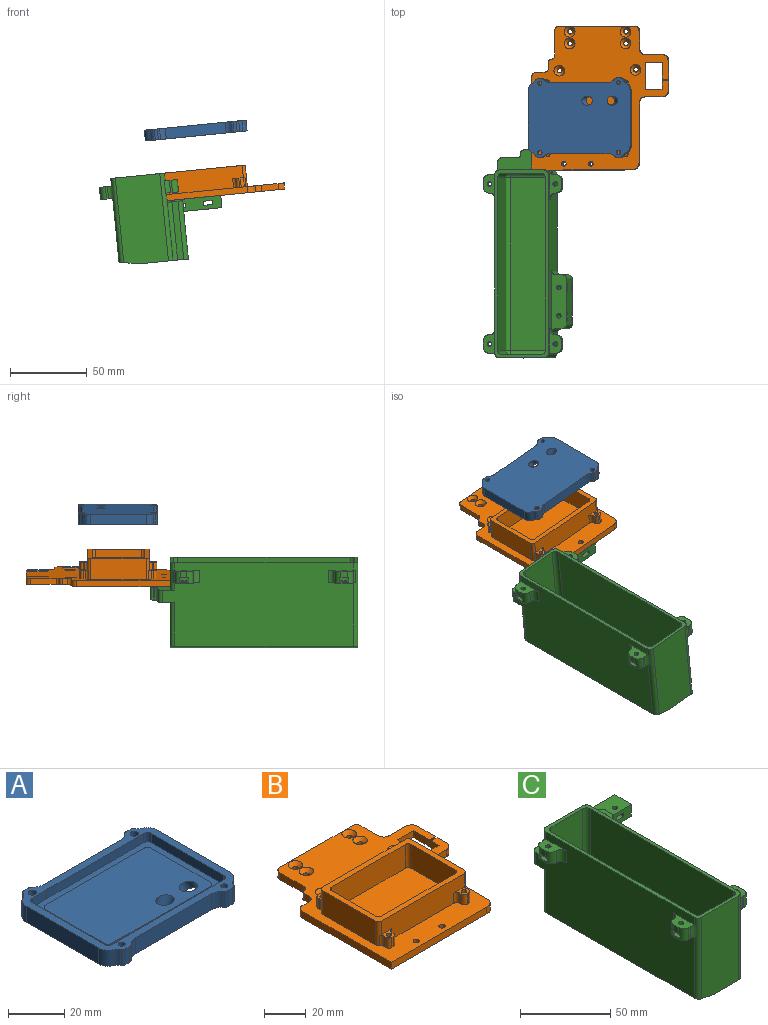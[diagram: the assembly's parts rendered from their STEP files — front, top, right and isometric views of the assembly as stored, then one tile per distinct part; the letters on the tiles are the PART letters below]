
ASSEMBLY  parts=3 mates=2
PART A: 55 faces, bbox 66.4x51.5x10 mm
  f0: plane 60.4x40.4mm, normal (0,0,1), area 653.3mm2, adj f1,f2,f3,f4,f5,f6,f7,f8
  f1: plane 7.5x4mm, normal (0,-1,0), area 30mm2, adj f0,f2,f31,f34
  f2: plane 48.9x4mm, normal (0,-1,0), area 195.6mm2, adj f0,f1,f3,f34
  f3: cylinder r=2mm len=4mm, axis (0,0,-1), area 12.6mm2, adj f0,f2,f4,f34
  f4: plane 36.4x4mm, normal (-1,0,0), area 145.6mm2, adj f0,f3,f5,f34
  f5: cylinder r=2mm len=4mm, axis (0,0,-1), area 12.6mm2, adj f0,f4,f6,f34
  f6: plane 56.4x4mm, normal (0,1,0), area 225.6mm2, adj f0,f5,f7,f34
  f7: cylinder r=2mm len=4mm, axis (0,0,-1), area 12.6mm2, adj f0,f6,f8,f34
  f8: plane 36.4x4mm, normal (1,0,0), area 145.6mm2, adj f0,f7,f31,f34
  f9: plane 39.03x7mm, normal (0,1,0), area 273.2mm2, adj f34,f35,f45,f46
  f10: cylinder r=2mm len=7mm, axis (0,0,-1), area 11.7mm2, adj f11,f34,f35,f46
  f11: plane 7x2mm, normal (0,1,0), area 14mm2, adj f10,f12,f34,f35
  f12: cylinder r=2mm len=7mm, axis (0,0,-1), area 14.3mm2, adj f11,f34,f35,f47
  f13: cylinder r=5mm len=7mm, axis (0,0,-1), area 38.7mm2, adj f14,f34,f35,f47
  f14: plane 36.4x7mm, normal (-1,0,0), area 254.8mm2, adj f13,f15,f34,f35
  f15: cylinder r=5mm len=7mm, axis (0,0,-1), area 38.7mm2, adj f14,f34,f35,f48
  f16: cylinder r=2mm len=7mm, axis (0,0,-1), area 14.3mm2, adj f17,f34,f35,f48
  f17: plane 7x2mm, normal (0,-1,0), area 14mm2, adj f16,f18,f34,f35
  f18: cylinder r=2mm len=7mm, axis (0,0,-1), area 11.7mm2, adj f17,f34,f35,f49
  f19: plane 38.61x7mm, normal (0,-1,0), area 270.3mm2, adj f34,f35,f49,f50
  f20: cylinder r=2mm len=7mm, axis (0,0,-1), area 13mm2, adj f21,f34,f35,f50
  f21: plane 7x2mm, normal (0,-1,0), area 14mm2, adj f20,f22,f34,f35
  f22: cylinder r=2mm len=7mm, axis (0,0,-1), area 15.9mm2, adj f21,f34,f35,f51
  f23: cylinder r=5mm len=7mm, axis (0,0,-1), area 37.3mm2, adj f24,f34,f35,f51
  f24: plane 36.4x7mm, normal (1,0,0), area 254.8mm2, adj f23,f25,f34,f35
  f25: cylinder r=5mm len=7mm, axis (0,0,-1), area 38.7mm2, adj f24,f34,f35,f52
  f26: cylinder r=2mm len=7mm, axis (0,0,-1), area 14.3mm2, adj f27,f34,f35,f52
  f27: plane 7x2mm, normal (0,1,0), area 14mm2, adj f26,f32,f34,f35
  f28: cylinder r=1.25mm len=7mm, axis (0,0,-1), area 55mm2, adj f34,f35
  f29: cylinder r=1.25mm len=7mm, axis (0,0,-1), area 55mm2, adj f34,f35
  f30: cylinder r=1.5mm len=7mm, axis (0,0,-1), area 66mm2, adj f34,f35
  f31: cylinder r=2mm len=4mm, axis (0,0,-1), area 12.6mm2, adj f0,f1,f8,f34
  f32: cylinder r=2mm len=7mm, axis (0,0,-1), area 11.7mm2, adj f27,f34,f35,f45
  f33: cylinder r=1.5mm len=7mm, axis (0,0,-1), area 66mm2, adj f34,f35
  f34: plane 66.4x51.5mm, normal (0,0,1), area 658.1mm2, adj f1,f2,f3,f4,f5,f6,f7,f8
  f35: plane 66.4x51.5mm, normal (0,0,-1), area 3029.5mm2, adj f9,f10,f11,f12,f13,f14,f15,f16
  f36: plane 29.4x1mm, normal (-1,0,0), area 29.4mm2, adj f0,f37,f43,f44
  f37: cylinder r=2mm len=2mm, axis (0,0,-1), area 3.1mm2, adj f0,f36,f38,f44
  f38: plane 49.5x1mm, normal (0,-1,0), area 49.5mm2, adj f0,f37,f39,f44
  f39: cylinder r=2mm len=2mm, axis (0,0,-1), area 3.1mm2, adj f0,f38,f40,f44
  f40: plane 29.4x1mm, normal (1,0,0), area 29.4mm2, adj f0,f39,f41,f44
  f41: cylinder r=2mm len=2mm, axis (0,0,-1), area 3.1mm2, adj f0,f40,f42,f44
  f42: plane 49.5x1mm, normal (0,1,0), area 49.5mm2, adj f0,f41,f43,f44
  f43: cylinder r=2mm len=2mm, axis (0,0,-1), area 3.1mm2, adj f0,f36,f42,f44
  f44: plane 53.5x33.4mm, normal (0,0,1), area 1718.2mm2, adj f36,f37,f38,f39,f40,f41,f42,f43
  f45: cylinder r=5mm len=7mm, axis (0,0,-1), area 29.2mm2, adj f9,f32,f34,f35
  f46: cylinder r=5mm len=7mm, axis (0,0,-1), area 29.2mm2, adj f9,f10,f34,f35
  f47: cylinder r=5mm len=7mm, axis (0,0,1), area 19.6mm2, adj f12,f13,f34,f35
  f48: cylinder r=5mm len=7mm, axis (0,0,1), area 19.6mm2, adj f15,f16,f34,f35
  f49: cylinder r=5mm len=7mm, axis (0,0,-1), area 29.2mm2, adj f18,f19,f34,f35
  f50: cylinder r=5mm len=7mm, axis (0,0,-1), area 32.5mm2, adj f19,f20,f34,f35
  f51: cylinder r=5mm len=7mm, axis (0,0,1), area 22.1mm2, adj f22,f23,f34,f35
  f52: cylinder r=5mm len=7mm, axis (0,0,1), area 19.6mm2, adj f25,f26,f34,f35
  f53: cylinder r=3mm len=10.02mm, axis (0.5,0,-0.87), area 87.1mm2, adj f35,f44
  f54: cylinder r=3mm len=10.02mm, axis (-0.5,0,-0.87), area 87.1mm2, adj f35,f44
PART B: 103 faces, bbox 89x93.5x18 mm
  f0: plane 93.5x89mm, normal (0,0,-1), area 6273mm2, adj f1,f3,f4,f5,f6,f10,f11,f12
  f1: plane 12x4mm, normal (1,0,0), area 43.4mm2, adj f0,f2,f92,f98
  f2: plane 93.5x89mm, normal (0,0,1), area 3705.7mm2, adj f1,f3,f4,f5,f6,f10,f11,f12
  f3: plane 11x4mm, normal (-1,0,0), area 39.4mm2, adj f0,f2,f95,f98
  f4: plane 38.5x4mm, normal (1,0,0), area 154mm2, adj f0,f2,f88,f102
  f5: plane 4x3.5mm, normal (-1,0,0), area 14mm2, adj f0,f2,f13,f76
  f6: plane 17.5x4mm, normal (1,0,0), area 70mm2, adj f0,f2,f87,f95
  f7: plane 8x5.27mm, normal (0,0,1), area 19.6mm2, adj f25,f53,f54,f55,f56,f57,f58,f59
  f8: plane 8x5.27mm, normal (0,0,1), area 19.6mm2, adj f43,f44,f45,f46,f47,f48,f49,f50
  f9: plane 8x5.27mm, normal (0,0,1), area 19.6mm2, adj f25,f26,f27,f28,f29,f30,f31,f32
  f10: plane 49x4mm, normal (0,1,0), area 196mm2, adj f0,f2,f11,f23
  f11: cylinder r=3mm len=4mm, axis (0,0,-1), area 18.8mm2, adj f0,f2,f10,f12
  f12: plane 16.5x4mm, normal (-1,0,0), area 66mm2, adj f0,f2,f11,f77
  f13: cylinder r=3mm len=4mm, axis (0,0,-1), area 18.8mm2, adj f0,f2,f5,f14
  f14: plane 5x4mm, normal (0,1,0), area 20mm2, adj f0,f2,f13,f15
  f15: cylinder r=3mm len=4mm, axis (0,0,-1), area 18.8mm2, adj f0,f2,f14,f16
  f16: plane 60.5x4mm, normal (-1,0,0), area 242mm2, adj f0,f2,f15,f78
  f17: plane 11.5x4mm, normal (1,0,0), area 46mm2, adj f0,f2,f23,f94
  f18: cylinder r=1.5mm len=3mm, axis (0,0,-1), area 18.8mm2, adj f0,f81
  f19: cylinder r=1.5mm len=3mm, axis (0,0,-1), area 18.8mm2, adj f0,f84
  f20: cylinder r=1.5mm len=3mm, axis (0,0,-1), area 18.8mm2, adj f0,f85
  f21: cylinder r=1.5mm len=3mm, axis (0,0,-1), area 18.8mm2, adj f0,f82
  f22: cylinder r=1.5mm len=3mm, axis (0,0,-1), area 18.8mm2, adj f0,f83
  f23: cylinder r=3mm len=4mm, axis (0,0,-1), area 18.8mm2, adj f0,f2,f10,f17
  f24: cylinder r=1.5mm len=3mm, axis (0,0,-1), area 18.8mm2, adj f0,f86
  f25: plane 56x14mm, normal (0,1,0), area 700mm2, adj f2,f7,f9,f26,f33,f53,f63,f66
  f26: cylinder r=2mm len=6mm, axis (0,0,-1), area 18.8mm2, adj f2,f9,f25,f27
  f27: plane 6x1mm, normal (1,0,0), area 6mm2, adj f2,f9,f26,f28
  f28: cylinder r=2mm len=6mm, axis (0,0,-1), area 18.8mm2, adj f2,f9,f27,f29
  f29: plane 6x1mm, normal (0,1,0), area 6mm2, adj f2,f9,f28,f30
  f30: cylinder r=2mm len=6mm, axis (0,0,-1), area 18.8mm2, adj f2,f9,f29,f31
  f31: plane 6x1.54mm, normal (-1,0,0), area 9.2mm2, adj f2,f9,f30,f32
  f32: cylinder r=2mm len=6mm, axis (0,0,-1), area 12.6mm2, adj f2,f9,f31,f33
  f33: cylinder r=2mm len=14mm, axis (0,0,-1), area 37.7mm2, adj f2,f9,f25,f32,f34,f66
  f34: plane 36x14mm, normal (-1,0,0), area 504mm2, adj f2,f33,f35,f66
  f35: cylinder r=2mm len=14mm, axis (0,0,-1), area 37.7mm2, adj f2,f34,f36,f43,f65,f66
  f36: cylinder r=2mm len=6mm, axis (0,0,-1), area 12.6mm2, adj f2,f35,f37,f65
  f37: plane 6x1.54mm, normal (-1,0,0), area 9.2mm2, adj f2,f36,f38,f65
  f38: cylinder r=2mm len=6mm, axis (0,0,-1), area 18.8mm2, adj f2,f37,f39,f65
  f39: plane 6x1mm, normal (0,-1,0), area 6mm2, adj f2,f38,f40,f65
  f40: cylinder r=2mm len=6mm, axis (0,0,-1), area 18.8mm2, adj f2,f39,f41,f65
  f41: plane 6x1mm, normal (1,0,0), area 6mm2, adj f2,f40,f42,f65
  f42: cylinder r=2mm len=6mm, axis (0,0,-1), area 18.8mm2, adj f2,f41,f43,f65
  f43: plane 56x14mm, normal (0,-1,0), area 700mm2, adj f2,f8,f35,f42,f44,f51,f65,f66
  f44: cylinder r=2mm len=6mm, axis (0,0,-1), area 18.8mm2, adj f2,f8,f43,f45
  f45: plane 6x1mm, normal (-1,0,0), area 6mm2, adj f2,f8,f44,f46
  f46: cylinder r=2mm len=6mm, axis (0,0,-1), area 18.8mm2, adj f2,f8,f45,f47
  f47: plane 6x1mm, normal (0,-1,0), area 6mm2, adj f2,f8,f46,f48
  f48: cylinder r=2mm len=6mm, axis (0,0,-1), area 18.8mm2, adj f2,f8,f47,f49
  f49: plane 6x1.54mm, normal (1,0,0), area 9.2mm2, adj f2,f8,f48,f50
  f50: cylinder r=2mm len=6mm, axis (0,0,-1), area 12.6mm2, adj f2,f8,f49,f51
  f51: cylinder r=2mm len=14mm, axis (0,0,-1), area 37.7mm2, adj f2,f8,f43,f50,f52,f66
  f52: plane 36x14mm, normal (1,0,0), area 504mm2, adj f2,f51,f53,f66
  f53: cylinder r=2mm len=14mm, axis (0,0,-1), area 37.7mm2, adj f2,f7,f25,f52,f54,f66
  f54: cylinder r=2mm len=6mm, axis (0,0,-1), area 12.6mm2, adj f2,f7,f53,f55
  f55: plane 6x1.54mm, normal (1,0,0), area 9.2mm2, adj f2,f7,f54,f56
  f56: cylinder r=2mm len=6mm, axis (0,0,-1), area 18.8mm2, adj f2,f7,f55,f57
  f57: plane 6x1mm, normal (0,1,0), area 6mm2, adj f2,f7,f56,f58
  f58: cylinder r=2mm len=6mm, axis (0,0,-1), area 18.8mm2, adj f2,f7,f57,f59
  f59: plane 6x1mm, normal (-1,0,0), area 6mm2, adj f2,f7,f58,f63
  f60: cylinder r=1.25mm len=10mm, axis (0,0,-1), area 78.5mm2, adj f0,f65
  f61: cylinder r=1.25mm len=10mm, axis (0,0,-1), area 78.5mm2, adj f0,f8
  f62: cylinder r=1.25mm len=10mm, axis (0,0,-1), area 78.5mm2, adj f0,f7
  f63: cylinder r=2mm len=6mm, axis (0,0,-1), area 18.8mm2, adj f2,f7,f25,f59
  f64: cylinder r=1.25mm len=10mm, axis (0,0,-1), area 78.5mm2, adj f0,f9
  f65: plane 8x5.27mm, normal (0,0,1), area 19.6mm2, adj f35,f36,f37,f38,f39,f40,f41,f42
  f66: plane 60x40mm, normal (0,0,1), area 564mm2, adj f25,f33,f34,f35,f43,f51,f52,f53
  f67: plane 54x34mm, normal (0,0,1), area 1736.6mm2, adj f68,f69,f70,f71,f72,f73,f74,f75
  f68: plane 50x18mm, normal (0,1,0), area 748mm2, adj f0,f66,f67,f69,f75,f99,f101
  f69: cylinder r=2mm len=14mm, axis (0,0,-1), area 44mm2, adj f66,f67,f68,f70
  f70: plane 30x14mm, normal (-1,0,0), area 420mm2, adj f66,f67,f69,f71
  f71: cylinder r=2mm len=14mm, axis (0,0,-1), area 44mm2, adj f66,f67,f70,f72
  f72: plane 50x14mm, normal (0,-1,0), area 700mm2, adj f66,f67,f71,f73
  f73: cylinder r=2mm len=14mm, axis (0,0,-1), area 44mm2, adj f66,f67,f72,f74
  f74: plane 30x14mm, normal (1,0,0), area 420mm2, adj f66,f67,f73,f75
  f75: cylinder r=2mm len=14mm, axis (0,0,-1), area 44mm2, adj f66,f67,f68,f74
  f76: cylinder r=2mm len=4mm, axis (0,0,1), area 12.6mm2, adj f0,f2,f5,f77
  f77: cylinder r=2mm len=4mm, axis (0,0,1), area 12.6mm2, adj f0,f2,f12,f76
  f78: plane 65x4mm, normal (0,-1,0), area 260mm2, adj f0,f2,f16,f102
  f79: cylinder r=1.5mm len=4mm, axis (0,0,1), area 37.7mm2, adj f0,f2
  f80: cylinder r=1.5mm len=4mm, axis (0,0,1), area 37.7mm2, adj f0,f2
  f81: cone r=1.5mm half-angle=45deg, axis (0,0,1), area 44.4mm2, adj f2,f18
  f82: cone r=1.5mm half-angle=45deg, axis (0,0,1), area 44.4mm2, adj f2,f21
  f83: cone r=1.5mm half-angle=45deg, axis (0,0,1), area 44.4mm2, adj f2,f22
  f84: cone r=1.5mm half-angle=45deg, axis (0,0,1), area 44.4mm2, adj f2,f19
  f85: cone r=1.5mm half-angle=45deg, axis (0,0,1), area 44.4mm2, adj f2,f20
  f86: cone r=1.5mm half-angle=45deg, axis (0,0,1), area 44.4mm2, adj f2,f24
  f87: plane 11x4mm, normal (0,1,0), area 44mm2, adj f0,f2,f6,f96
  f88: cylinder r=4mm len=4mm, axis (0,0,1), area 25.1mm2, adj f0,f2,f4,f89
  f89: plane 11x4mm, normal (0,-1,0), area 44mm2, adj f0,f2,f88,f90
  f90: cylinder r=4mm len=4mm, axis (0,0,1), area 25.1mm2, adj f0,f2,f89,f91
  f91: plane 8.65x4mm, normal (1,0,0), area 30mm2, adj f0,f2,f90,f97
  f92: cylinder r=4mm len=4mm, axis (0,0,1), area 25.1mm2, adj f0,f1,f2,f93
  f93: plane 11x4mm, normal (0,1,0), area 44mm2, adj f0,f2,f92,f94
  f94: cylinder r=4mm len=4mm, axis (0,0,1), area 25.1mm2, adj f0,f2,f17,f93
  f95: plane 11x4mm, normal (0,-1,0), area 44mm2, adj f0,f2,f3,f6
  f96: plane 7.65x4mm, normal (-1,0,0), area 26mm2, adj f0,f2,f87,f97
  f97: plane 4x4mm, normal (0,0.87,0.5), area 18.5mm2, adj f0,f2,f91,f96
  f98: plane 4x4mm, normal (0,-0.87,-0.5), area 18.5mm2, adj f0,f1,f2,f3
  f99: plane 8x4mm, normal (-1,0,0), area 32mm2, adj f0,f67,f68,f100
  f100: plane 12x4mm, normal (0,-1,0), area 48mm2, adj f0,f67,f99,f101
  f101: plane 8x4mm, normal (1,0,0), area 32mm2, adj f0,f67,f68,f100
  f102: cylinder r=5mm len=5mm, axis (0,0,1), area 31.4mm2, adj f0,f2,f4,f78
PART C: 159 faces, bbox 78x135x57 mm
  f0: plane 38x29mm, normal (1,0,0), area 1040.4mm2, adj f29,f50,f51,f52,f53,f57,f58,f59
  f1: plane 31x29mm, normal (0,1,0), area 747.9mm2, adj f20,f29,f32,f78,f129,f150,f151,f152
  f2: plane 4.3x4mm, normal (-1,0,0), area 17.2mm2, adj f4,f5,f106,f148
  f3: plane 4x1mm, normal (-1,0,0), area 4mm2, adj f7,f8,f114,f142
  f4: cylinder r=4mm len=8mm, axis (0,0,-1), area 48mm2, adj f2,f102,f103,f106,f107,f145,f147,f148
  f5: cylinder r=4mm len=8mm, axis (0,0,-1), area 48mm2, adj f2,f103,f105,f106,f107,f146,f147,f148
  f6: cylinder r=1.5mm len=3mm, axis (0,0,-1), area 9.4mm2, adj f107,f147
  f7: cylinder r=4mm len=8mm, axis (0,0,-1), area 48mm2, adj f3,f110,f111,f113,f114,f140,f142,f143
  f8: cylinder r=4mm len=8mm, axis (0,0,-1), area 48mm2, adj f3,f108,f111,f113,f114,f141,f142,f143
  f9: cylinder r=1.5mm len=3mm, axis (0,0,-1), area 9.4mm2, adj f114,f142
  f10: plane 4.3x4mm, normal (1,0,0), area 17.2mm2, adj f12,f13,f115,f138
  f11: plane 4x1mm, normal (1,0,0), area 4mm2, adj f15,f17,f123,f131
  f12: cylinder r=4mm len=8mm, axis (0,0,-1), area 48mm2, adj f10,f115,f116,f118,f119,f135,f137,f138
  f13: cylinder r=4mm len=8mm, axis (0,0,-1), area 48mm2, adj f10,f115,f116,f119,f121,f136,f137,f138
  f14: cylinder r=1.5mm len=3mm, axis (0,0,-1), area 9.4mm2, adj f116,f137
  f15: cylinder r=4mm len=8mm, axis (0,0,-1), area 48mm2, adj f11,f122,f123,f124,f125,f130,f131,f132
  f16: cylinder r=1.5mm len=3mm, axis (0,0,-1), area 9.4mm2, adj f123,f131
  f17: cylinder r=4mm len=8mm, axis (0,0,-1), area 48mm2, adj f11,f122,f123,f124,f127,f131,f132,f133
  f18: plane 57x29mm, normal (0,-1,0), area 1644.2mm2, adj f21,f29,f80,f83,f129
  f19: plane 124x54.71mm, normal (-1,0,0), area 6154.1mm2, adj f20,f21,f30,f32,f79,f82,f83,f105
  f20: cylinder r=3mm len=29.24mm, axis (0,0,1), area 136.2mm2, adj f1,f19,f32,f129
  f21: cylinder r=3mm len=55.24mm, axis (0,0,-1), area 244.1mm2, adj f18,f19,f83,f109,f113,f114,f129
  f22: plane 35x8mm, normal (0,-1,0), area 249.2mm2, adj f27,f30,f31,f32,f36,f37,f38,f39
  f23: cylinder r=1.5mm len=3mm, axis (0,0,1), area 25mm2, adj f32,f40
  f24: cylinder r=1.5mm len=3mm, axis (0,0,1), area 25mm2, adj f32,f36
  f25: plane 53x8mm, normal (0,1,0), area 393.2mm2, adj f30,f31,f32,f36,f37,f38,f39,f40
  f26: plane 10x8mm, normal (0,1,0), area 80mm2, adj f30,f32,f44,f79
  f27: plane 119x57mm, normal (1,0,0), area 4822mm2, adj f22,f29,f30,f32,f74,f75,f78,f80
  f28: plane 29x18mm, normal (0,1,0), area 522mm2, adj f30,f81,f82,f83
  f29: plane 122x32mm, normal (0,0,-1), area 3030.1mm2, adj f0,f1,f18,f27,f46,f47,f74,f75
  f30: plane 70x16mm, normal (0,0,1), area 822.8mm2, adj f19,f22,f25,f26,f27,f28,f31,f33
  f31: plane 13x8mm, normal (1,0,0), area 104mm2, adj f22,f25,f30,f32
  f32: plane 70x16mm, normal (0,0,-1), area 822.8mm2, adj f1,f19,f20,f22,f23,f24,f25,f26
  f33: cylinder r=1.5mm len=3mm, axis (0,0,1), area 25mm2, adj f30,f42
  f34: cylinder r=1.5mm len=3mm, axis (0,0,1), area 25mm2, adj f30,f38
  f35: plane 8x1mm, normal (-1,0,0), area 8mm2, adj f30,f32,f44,f45
  f36: plane 13x5.7mm, normal (0,0,1), area 67mm2, adj f22,f24,f25,f37,f39
  f37: plane 13x2.7mm, normal (1,0,0), area 35.1mm2, adj f22,f25,f36,f38
  f38: plane 13x5.7mm, normal (0,0,-1), area 67mm2, adj f22,f25,f34,f37,f39
  f39: plane 13x2.7mm, normal (-1,0,0), area 35.1mm2, adj f22,f25,f36,f38
  f40: plane 13x5.7mm, normal (0,0,1), area 67mm2, adj f22,f23,f25,f41,f43
  f41: plane 13x2.7mm, normal (1,0,0), area 35.1mm2, adj f22,f25,f40,f42
  f42: plane 13x5.7mm, normal (0,0,-1), area 67mm2, adj f22,f25,f33,f41,f43
  f43: plane 13x2.7mm, normal (-1,0,0), area 35.1mm2, adj f22,f25,f40,f42
  f44: cylinder r=2mm len=8mm, axis (0,0,1), area 25.1mm2, adj f26,f30,f32,f35
  f45: cylinder r=2mm len=8mm, axis (0,0,-1), area 25.1mm2, adj f25,f30,f32,f35
  f46: plane 38x4mm, normal (0,1,0), area 152mm2, adj f29,f75,f77,f158
  f47: plane 38x4mm, normal (0,-1,0), area 152mm2, adj f29,f74,f76,f158
  f48: cylinder r=1.5mm len=4mm, axis (0,0,1), area 37.7mm2, adj f58,f158
  f49: cylinder r=1.5mm len=4mm, axis (0,0,1), area 37.7mm2, adj f51,f158
  f50: plane 8x5.7mm, normal (0,0,1), area 38.5mm2, adj f0,f52,f53,f54,f56
  f51: plane 8x5.7mm, normal (0,0,-1), area 38.5mm2, adj f0,f49,f52,f53,f54
  f52: plane 8x2.7mm, normal (0,-1,0), area 21.6mm2, adj f0,f50,f51,f54
  f53: plane 8x2.7mm, normal (0,1,0), area 21.6mm2, adj f0,f50,f51,f54
  f54: plane 5.7x2.7mm, normal (1,0,0), area 15.4mm2, adj f50,f51,f52,f53
  f55: plane 3x3mm, normal (0,0,1), area 7.1mm2, adj f56
  f56: cylinder r=1.5mm len=17.3mm, axis (0,0,1), area 163mm2, adj f50,f55
  f57: plane 8x5.7mm, normal (0,0,1), area 38.5mm2, adj f0,f59,f60,f61,f63
  f58: plane 8x5.7mm, normal (0,0,-1), area 38.5mm2, adj f0,f48,f59,f60,f61
  f59: plane 8x2.7mm, normal (0,-1,0), area 21.6mm2, adj f0,f57,f58,f61
  f60: plane 8x2.7mm, normal (0,1,0), area 21.6mm2, adj f0,f57,f58,f61
  f61: plane 5.7x2.7mm, normal (1,0,0), area 15.4mm2, adj f57,f58,f59,f60
  f62: plane 3x3mm, normal (0,0,1), area 7.1mm2, adj f63
  f63: cylinder r=1.5mm len=17.3mm, axis (0,0,1), area 163mm2, adj f57,f62
  f64: plane 8x5.7mm, normal (0,0,1), area 45.6mm2, adj f0,f65,f67,f68
  f65: plane 8x2.7mm, normal (0,-1,0), area 21.6mm2, adj f0,f64,f66,f68
  f66: plane 8x5.7mm, normal (0,0,-1), area 45.6mm2, adj f0,f65,f67,f68
  f67: plane 8x2.7mm, normal (0,1,0), area 21.6mm2, adj f0,f64,f66,f68
  f68: plane 5.7x2.7mm, normal (1,0,0), area 15.4mm2, adj f64,f65,f66,f67
  f69: plane 8x5.7mm, normal (0,0,1), area 45.6mm2, adj f0,f70,f72,f73
  f70: plane 8x2.7mm, normal (0,-1,0), area 21.6mm2, adj f0,f69,f71,f73
  f71: plane 8x5.7mm, normal (0,0,-1), area 45.6mm2, adj f0,f70,f72,f73
  f72: plane 8x2.7mm, normal (0,1,0), area 21.6mm2, adj f0,f69,f71,f73
  f73: plane 5.7x2.7mm, normal (1,0,0), area 15.4mm2, adj f69,f70,f71,f72
  f74: cylinder r=3mm len=38mm, axis (0,0,1), area 179.1mm2, adj f27,f29,f47,f158
  f75: cylinder r=3mm len=38mm, axis (0,0,-1), area 179.1mm2, adj f27,f29,f46,f158
  f76: cylinder r=3mm len=38mm, axis (0,0,1), area 179.1mm2, adj f0,f29,f47,f158
  f77: cylinder r=3mm len=38mm, axis (0,0,-1), area 179.1mm2, adj f0,f29,f46,f158
  f78: cylinder r=3mm len=31mm, axis (0,0,-1), area 146.1mm2, adj f1,f27,f29,f32
  f79: cylinder r=3mm len=8mm, axis (0,0,-1), area 37.7mm2, adj f19,f26,f30,f32
  f80: cylinder r=3mm len=57mm, axis (0,0,1), area 254mm2, adj f18,f27,f29,f83,f115,f116,f117
  f81: cylinder r=3mm len=18mm, axis (0,0,-1), area 70.2mm2, adj f27,f28,f30,f83,f122,f123,f126
  f82: cylinder r=3mm len=18mm, axis (0,0,1), area 70.2mm2, adj f19,f28,f30,f83,f101,f106,f107
  f83: plane 122x35mm, normal (0,0,1), area 612mm2, adj f18,f19,f21,f27,f28,f80,f81,f82
  f84: plane 112x25mm, normal (0,0,1), area 2800mm2, adj f85,f87,f89,f91
  f85: cylinder r=3mm len=112mm, axis (0,1,0), area 527.8mm2, adj f84,f86,f92,f100
  f86: sphere r=3mm, area 14.1mm2, adj f85,f87,f99
  f87: cylinder r=3mm len=25mm, axis (1,0,0), area 117.8mm2, adj f84,f86,f88,f98
  f88: sphere r=3mm, area 14.1mm2, adj f87,f89,f97
  f89: cylinder r=3mm len=112mm, axis (0,-1,0), area 527.8mm2, adj f84,f88,f90,f96
  f90: sphere r=3mm, area 13.5mm2, adj f89,f91,f95,f153
  f91: cylinder r=3mm len=25mm, axis (-1,0,0), area 100.9mm2, adj f84,f90,f92,f94,f150,f151,f153
  f92: sphere r=3mm, area 14.1mm2, adj f85,f91,f93
  f93: cylinder r=3mm len=51mm, axis (0,0,1), area 240.3mm2, adj f83,f92,f94,f100
  f94: plane 51x25mm, normal (0,-1,0), area 1160.5mm2, adj f83,f91,f93,f95,f151,f154,f155,f156
  f95: cylinder r=3mm len=51mm, axis (0,0,-1), area 228.6mm2, adj f83,f90,f94,f96,f152,f153,f154
  f96: plane 112x51mm, normal (1,0,0), area 5712mm2, adj f83,f89,f95,f97
  f97: cylinder r=3mm len=51mm, axis (0,0,1), area 240.3mm2, adj f83,f88,f96,f98
  f98: plane 51x25mm, normal (0,1,0), area 1275mm2, adj f83,f87,f97,f99
  f99: cylinder r=3mm len=51mm, axis (0,0,-1), area 240.3mm2, adj f83,f86,f98,f100
  f100: plane 112x51mm, normal (-1,0,0), area 5712mm2, adj f83,f85,f93,f99
  f101: cylinder r=4mm len=8mm, axis (0,0,-1), area 30.8mm2, adj f82,f102,f106,f107
  f102: plane 8x1.26mm, normal (0,1,0), area 10mm2, adj f4,f101,f106,f107
  f103: plane 4x1mm, normal (-1,0,0), area 4mm2, adj f4,f5,f107,f147
  f104: cylinder r=1.5mm len=4.3mm, axis (0,0,-1), area 40.5mm2, adj f106,f148
  f105: cylinder r=4mm len=8mm, axis (0,0,-1), area 50.3mm2, adj f5,f19,f106,f107
  f106: plane 17.71x8.54mm, normal (0,0,1), area 86.5mm2, adj f2,f4,f5,f19,f82,f101,f102,f104
  f107: plane 17.71x8.54mm, normal (0,0,-1), area 86.5mm2, adj f4,f5,f6,f19,f82,f101,f102,f103
  f108: plane 8x1.26mm, normal (0,-1,0), area 10mm2, adj f8,f109,f113,f114
  f109: cylinder r=4mm len=8mm, axis (0,0,-1), area 30.8mm2, adj f21,f108,f113,f114
  f110: cylinder r=4mm len=8mm, axis (0,0,-1), area 50.3mm2, adj f7,f19,f113,f114
  f111: plane 4.3x4mm, normal (-1,0,0), area 17.2mm2, adj f7,f8,f113,f143
  f112: cylinder r=1.5mm len=4.3mm, axis (0,0,-1), area 40.5mm2, adj f113,f143
  f113: plane 17.71x8.54mm, normal (0,0,1), area 86.5mm2, adj f7,f8,f19,f21,f108,f109,f110,f111
  f114: plane 17.71x8.54mm, normal (0,0,-1), area 86.5mm2, adj f3,f7,f8,f9,f19,f21,f108,f109
  f115: plane 17.71x8.54mm, normal (0,0,1), area 86.5mm2, adj f10,f12,f13,f27,f80,f117,f118,f120
  f116: plane 17.71x8.54mm, normal (0,0,-1), area 86.5mm2, adj f12,f13,f14,f27,f80,f117,f118,f119
  f117: cylinder r=4mm len=8mm, axis (0,0,-1), area 30.8mm2, adj f80,f115,f116,f118
  f118: plane 8x1.26mm, normal (0,-1,0), area 10mm2, adj f12,f115,f116,f117
  f119: plane 4x1mm, normal (1,0,0), area 4mm2, adj f12,f13,f116,f137
  f120: cylinder r=1.5mm len=4.3mm, axis (0,0,-1), area 40.5mm2, adj f115,f138
  f121: cylinder r=4mm len=8mm, axis (0,0,-1), area 50.3mm2, adj f13,f27,f115,f116
  f122: plane 17.71x8.54mm, normal (0,0,1), area 86.5mm2, adj f15,f17,f27,f81,f124,f125,f126,f127
  f123: plane 17.71x8.54mm, normal (0,0,-1), area 86.5mm2, adj f11,f15,f16,f17,f27,f81,f125,f126
  f124: plane 4.3x4mm, normal (1,0,0), area 17.2mm2, adj f15,f17,f122,f132
  f125: plane 8x1.26mm, normal (0,1,0), area 10mm2, adj f15,f122,f123,f126
  f126: cylinder r=4mm len=8mm, axis (0,0,-1), area 30.8mm2, adj f81,f122,f123,f125
  f127: cylinder r=4mm len=8mm, axis (0,0,-1), area 50.3mm2, adj f17,f27,f122,f123
  f128: cylinder r=1.5mm len=4.3mm, axis (0,0,-1), area 40.5mm2, adj f122,f132
  f129: plane 122x13mm, normal (-0.17,0,-0.98), area 1606.5mm2, adj f1,f18,f19,f20,f21,f29
  f130: plane 7.91x2.7mm, normal (0,-1,0), area 21.4mm2, adj f15,f131,f132,f134
  f131: plane 8x5.7mm, normal (0,0,1), area 38.5mm2, adj f11,f15,f16,f17,f130,f133,f134
  f132: plane 8x5.7mm, normal (0,0,-1), area 38.5mm2, adj f15,f17,f124,f128,f130,f133,f134
  f133: plane 7.91x2.7mm, normal (0,1,0), area 21.4mm2, adj f17,f131,f132,f134
  f134: plane 5.7x2.7mm, normal (1,0,0), area 15.4mm2, adj f130,f131,f132,f133
  f135: plane 7.91x2.7mm, normal (0,1,0), area 21.4mm2, adj f12,f137,f138,f139
  f136: plane 7.91x2.7mm, normal (0,-1,0), area 21.4mm2, adj f13,f137,f138,f139
  f137: plane 8x5.7mm, normal (0,0,1), area 38.5mm2, adj f12,f13,f14,f119,f135,f136,f139
  f138: plane 8x5.7mm, normal (0,0,-1), area 38.5mm2, adj f10,f12,f13,f120,f135,f136,f139
  f139: plane 5.7x2.7mm, normal (1,0,0), area 15.4mm2, adj f135,f136,f137,f138
  f140: plane 7.91x2.7mm, normal (0,-1,0), area 21.4mm2, adj f7,f142,f143,f144
  f141: plane 7.91x2.7mm, normal (0,1,0), area 21.4mm2, adj f8,f142,f143,f144
  f142: plane 8x5.7mm, normal (0,0,1), area 38.5mm2, adj f3,f7,f8,f9,f140,f141,f144
  f143: plane 8x5.7mm, normal (0,0,-1), area 38.5mm2, adj f7,f8,f111,f112,f140,f141,f144
  f144: plane 5.7x2.7mm, normal (-1,0,0), area 15.4mm2, adj f140,f141,f142,f143
  f145: plane 7.91x2.7mm, normal (0,-1,0), area 21.4mm2, adj f4,f147,f148,f149
  f146: plane 7.91x2.7mm, normal (0,1,0), area 21.4mm2, adj f5,f147,f148,f149
  f147: plane 8x5.7mm, normal (0,0,1), area 38.5mm2, adj f4,f5,f6,f103,f145,f146,f149
  f148: plane 8x5.7mm, normal (0,0,-1), area 38.5mm2, adj f2,f4,f5,f104,f145,f146,f149
  f149: plane 5.7x2.7mm, normal (-1,0,0), area 15.4mm2, adj f145,f146,f147,f148
  f150: plane 4x2.76mm, normal (0,0,1), area 11.1mm2, adj f1,f91,f151,f153
  f151: cylinder r=3mm len=3mm, axis (0,1,0), area 10.8mm2, adj f1,f91,f94,f150,f157
  f152: plane 9x2.17mm, normal (1,0,0), area 19.5mm2, adj f1,f95,f153,f154
  f153: cylinder r=3mm len=3mm, axis (0,1,0), area 11mm2, adj f1,f90,f91,f95,f150,f152
  f154: cylinder r=3mm len=3mm, axis (0,1,0), area 9.6mm2, adj f1,f94,f95,f152,f155
  f155: plane 4x2mm, normal (0,0,-1), area 8mm2, adj f1,f94,f154,f156
  f156: cylinder r=3mm len=3mm, axis (0,1,0), area 9.4mm2, adj f1,f94,f155,f157
  f157: plane 9x2mm, normal (-1,0,0), area 18mm2, adj f1,f94,f151,f156
  f158: plane 41x10mm, normal (0,0,1), area 335.9mm2, adj f0,f27,f46,f47,f48,f49,f74,f75
PLACE A rot(axis=(-1,0,-0.05),180deg) t=(10.63,4.52,-7.52)mm
PLACE B rot(axis=(0,-1,0),5.7deg) t=(22.1,57.03,-53.61)mm
PLACE C rot(axis=(0,-1,0),5.7deg) t=(-1.03,-11.01,-95.1)mm
MATE fastened B.f80 <-> C.f24  axis (0.1,0,-1) through (0.71,-24.97,-55.73)mm
MATE slider A.f31 <-> B.f35  axis (0.1,0,-1) through (-17.57,-13.47,-13.33)mm
